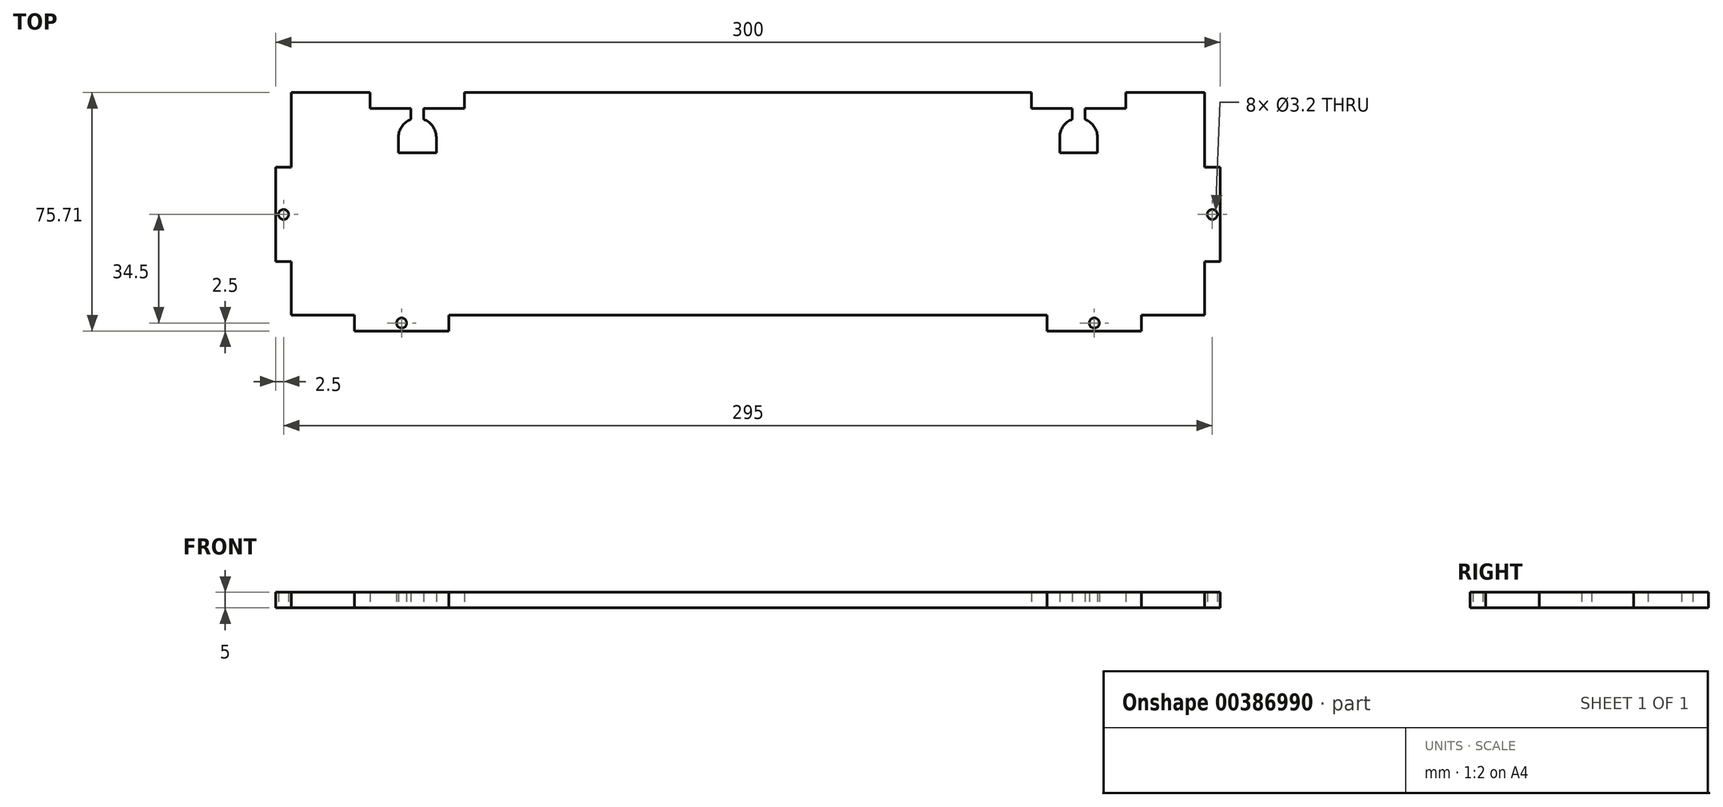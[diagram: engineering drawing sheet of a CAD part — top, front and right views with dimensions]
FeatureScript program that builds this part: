
annotation { "Feature Type Name" : "Feature", "Feature Type Description" : "" }
export const myFeature = defineFeature(function(context is Context, id is Id, definition is map)
    precondition{}
    {
        {
            var Q0;
            Q0=qCreatedBy(makeId("Top.planeOp"),FACE);
            var sketch = newSketch(context, id + "F0", { "sketchPlane" : qUnion([Q0])});
            skLineSegment(sketch, "E0.bottom", {"start": v(0, 0) * mm, "end": v(25, 0) * mm});
            skLineSegment(sketch, "E0.top", {"start": v(0, -70.71) * mm, "end": v(20, -70.71) * mm});
            skLineSegment(sketch, "E0.left", {"start": v(0, 0) * mm, "end": v(0, -23.7) * mm});
            skLineSegment(sketch, "E0.right", {"start": v(290, 0) * mm, "end": v(290, -23.7) * mm});
            skLineSegment(sketch, "E1", {"start": v(46, -19.16) * mm, "end": v(34, -19.16) * mm});
            skLineSegment(sketch, "E2", {"start": v(46, -19.16) * mm, "end": v(46, -14.16) * mm});
            skLineSegment(sketch, "E3", {"start": v(34, -19.16) * mm, "end": v(34, -14.16) * mm});
            skLineSegment(sketch, "E4", {"start": v(42, -5) * mm, "end": v(42, -8.5) * mm});
            skLineSegment(sketch, "E5", {"start": v(38, -5) * mm, "end": v(38, -8.5) * mm});
            skArc(sketch, "E6", {"start": v(46, -14.16) * mm, "mid": v(44.9, -10.7) * mm, "end": v(42, -8.5) * mm});
            skArc(sketch, "E7.trimOffspring", {"start": v(38, -8.5) * mm, "mid": v(35.1, -10.7) * mm, "end": v(34, -14.16) * mm});
            skLineSegment(sketch, "E8.bottom", {"start": v(55, 0) * mm, "end": v(55, -5) * mm});
            skLineSegment(sketch, "E8.top", {"start": v(25, 0) * mm, "end": v(25, -5) * mm});
            skLineSegment(sketch, "E8.right", {"start": v(55, -5) * mm, "end": v(42, -5) * mm});
            skLineSegment(sketch, "E9.trimOffspring", {"start": v(38, -5) * mm, "end": v(25, -5) * mm});
            skLineSegment(sketch, "E10", {"start": v(256, -19.16) * mm, "end": v(244, -19.16) * mm});
            skLineSegment(sketch, "E11", {"start": v(256, -19.16) * mm, "end": v(256, -14.16) * mm});
            skLineSegment(sketch, "E12", {"start": v(244, -19.16) * mm, "end": v(244, -14.16) * mm});
            skLineSegment(sketch, "E13", {"start": v(252, -5) * mm, "end": v(252, -8.5) * mm});
            skLineSegment(sketch, "E14", {"start": v(248, -5) * mm, "end": v(248, -8.5) * mm});
            skArc(sketch, "E15", {"start": v(256, -14.16) * mm, "mid": v(254.9, -10.7) * mm, "end": v(252, -8.5) * mm});
            skArc(sketch, "E16.trimOffspring", {"start": v(248, -8.5) * mm, "mid": v(245.1, -10.7) * mm, "end": v(244, -14.16) * mm});
            skLineSegment(sketch, "E17.bottom", {"start": v(265, 0) * mm, "end": v(265, -5) * mm});
            skLineSegment(sketch, "E17.top", {"start": v(235, 0) * mm, "end": v(235, -5) * mm});
            skLineSegment(sketch, "E17.right", {"start": v(265, -5) * mm, "end": v(252, -5) * mm});
            skLineSegment(sketch, "E18.trimOffspring", {"start": v(248, -5) * mm, "end": v(235, -5) * mm});
            skLineSegment(sketch, "E19.trimOffspring", {"start": v(55, 0) * mm, "end": v(235, 0) * mm});
            skLineSegment(sketch, "E20.trimOffspring", {"start": v(265, 0) * mm, "end": v(290, 0) * mm});
            skLineSegment(sketch, "E21.bottom", {"start": v(290, -53.7) * mm, "end": v(295, -53.7) * mm});
            skLineSegment(sketch, "E21.top", {"start": v(290, -23.7) * mm, "end": v(295, -23.7) * mm});
            skLineSegment(sketch, "E21.right", {"start": v(295, -53.7) * mm, "end": v(295, -23.7) * mm});
            skCircle(sketch, "E22", {"center": v(292.5, -38.7) * mm, "radius": 1.6 * mm});
            skPoint(sketch, "E22.centerSnap0", {"position": v(295, -38.7) * mm});
            skPoint(sketch, "E23", {"position": v(292.5, -53.7) * mm});
            skLineSegment(sketch, "E24.trimOffspring", {"start": v(290, -53.7) * mm, "end": v(290, -70.7) * mm});
            skLineSegment(sketch, "E25.bottom", {"start": v(0, -53.71) * mm, "end": v(-5, -53.71) * mm});
            skLineSegment(sketch, "E25.top", {"start": v(0, -23.71) * mm, "end": v(-5, -23.71) * mm});
            skLineSegment(sketch, "E25.right", {"start": v(-5, -53.71) * mm, "end": v(-5, -23.7) * mm});
            skLineSegment(sketch, "E26.trimOffspring", {"start": v(0, -53.71) * mm, "end": v(0, -70.71) * mm});
            skCircle(sketch, "E27", {"center": v(-2.5, -38.7) * mm, "radius": 1.6 * mm});
            skPoint(sketch, "E27.centerSnap0", {"position": v(-5, -38.7) * mm});
            skPoint(sketch, "E28", {"position": v(-2.5, -53.71) * mm});
            skLineSegment(sketch, "E29.top", {"start": v(20, -75.7) * mm, "end": v(50, -75.7) * mm});
            skLineSegment(sketch, "E29.left", {"start": v(20, -70.71) * mm, "end": v(20, -75.7) * mm});
            skLineSegment(sketch, "E29.right", {"start": v(50, -70.7) * mm, "end": v(50, -75.7) * mm});
            skLineSegment(sketch, "E30.top", {"start": v(240, -75.7) * mm, "end": v(270, -75.7) * mm});
            skLineSegment(sketch, "E30.left", {"start": v(240, -70.7) * mm, "end": v(240, -75.7) * mm});
            skLineSegment(sketch, "E30.right", {"start": v(270, -70.7) * mm, "end": v(270, -75.7) * mm});
            skLineSegment(sketch, "E31.trimOffspring", {"start": v(50, -70.7) * mm, "end": v(240, -70.7) * mm});
            skLineSegment(sketch, "E32.trimOffspring", {"start": v(270, -70.7) * mm, "end": v(290, -70.7) * mm});
            skCircle(sketch, "E33", {"center": v(35, -73.2) * mm, "radius": 1.6 * mm});
            skPoint(sketch, "E33.centerSnap0", {"position": v(35, -75.7) * mm});
            skCircle(sketch, "E34", {"center": v(255, -73.2) * mm, "radius": 1.6 * mm});
            skPoint(sketch, "E34.centerSnap0", {"position": v(255, -75.7) * mm});
            skPoint(sketch, "E35", {"position": v(240, -73.2) * mm});
            skPoint(sketch, "E36", {"position": v(50, -73.2) * mm});
            skSolve(sketch);
        }
        {
            var Q0;
            Q0=makeQuery(id+"F0.imprint","IMPRINT",FACE,{"disambiguationData":[TD([[makeQuery(id+"F0.imprint","IMPRINT",EDGE,{"derivedFrom":sQuery(id+"F0.wireOp",EDGE,"E0.bottom")}),-1.0]])]});
            extrude(context, id + "F1", {"entities" : qUnion([Q0]), "depth" : 5 * mm});
        }
    });
